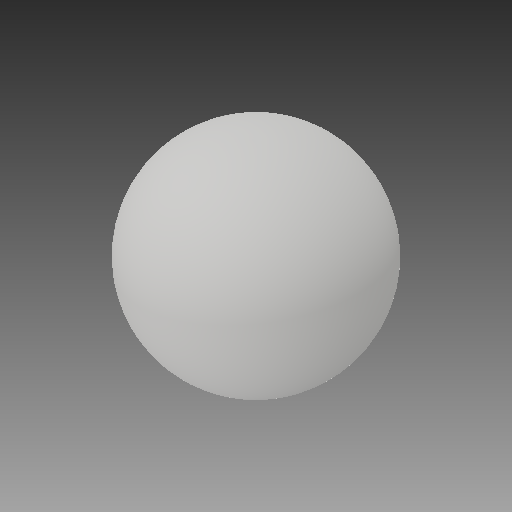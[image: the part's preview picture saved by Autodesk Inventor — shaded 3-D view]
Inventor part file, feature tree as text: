
AUTODESK INVENTOR PART (.ipt)
format: ipt  version: 2018 (Build 220112000, 112)  size: 110,592 bytes
history: native  units: in
note: dims shown in document units (in); Inventor stores cm internally (conversion verified against a paired STEP export)
features: revolve x1
ambient origin geometry x8: Origin, YZ Plane, XZ Plane, XY Plane, X Axis, Y Axis, Z Axis, Center Point
bodies: Solid1 (feature_tree)
feature tree (1):
  revolve  "Revolve2"  [1 undecoded]
note: 1 required parameter value undecoded (feature->parameter linkage not recoverable at this tier; creation-order binding heuristic only, values carry confidence <= 0.55)
